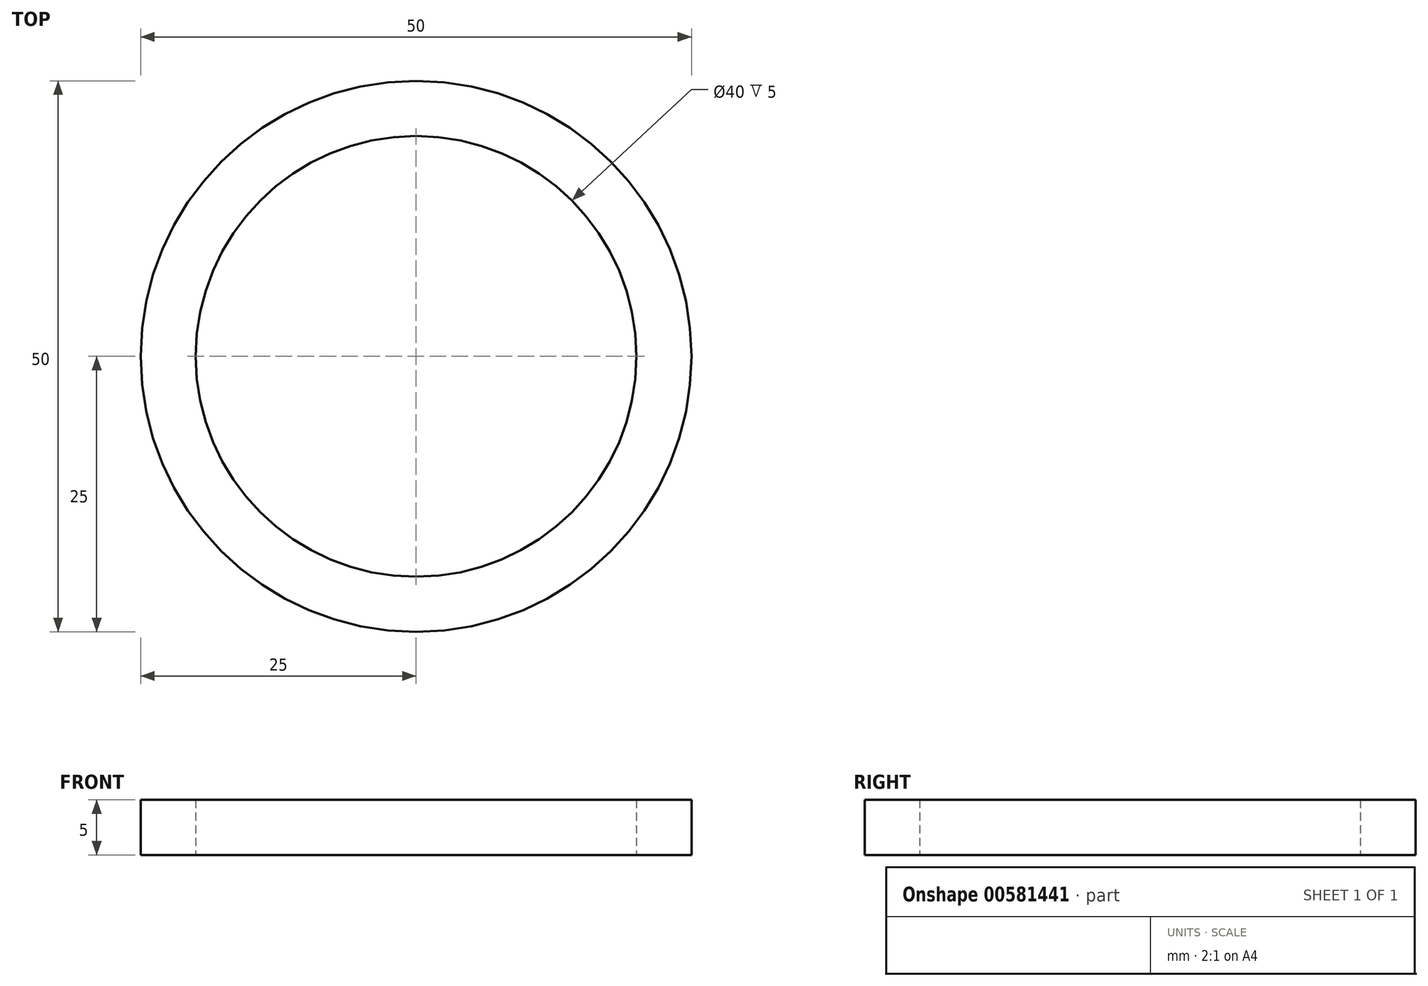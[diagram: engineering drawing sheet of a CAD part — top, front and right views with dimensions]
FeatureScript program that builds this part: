
annotation { "Feature Type Name" : "Feature", "Feature Type Description" : "" }
export const myFeature = defineFeature(function(context is Context, id is Id, definition is map)
    precondition{}
    {
        {
            var Q0;
            Q0=qCreatedBy(makeId("Top.planeOp"),FACE);
            var sketch = newSketch(context, id + "F0", { "sketchPlane" : qUnion([Q0])});
            skCircle(sketch, "E0", {"center": v(0, 0) * mm, "radius": 25 * mm});
            skCircle(sketch, "E1", {"center": v(0, 0) * mm, "radius": 20 * mm});
            skSolve(sketch);
        }
        {
            var Q0;
            Q0=makeQuery(id+"F0.imprint","IMPRINT",FACE,{"disambiguationData":[TD([[makeQuery(id+"F0.imprint","IMPRINT",EDGE,{"derivedFrom":sQuery(id+"F0.wireOp",EDGE,"E0")}),1.0]])]});
            extrude(context, id + "F1", {"entities" : qUnion([Q0]), "depth" : 5 * mm, "offsetDistance" : 25 * mm});
        }
    });
